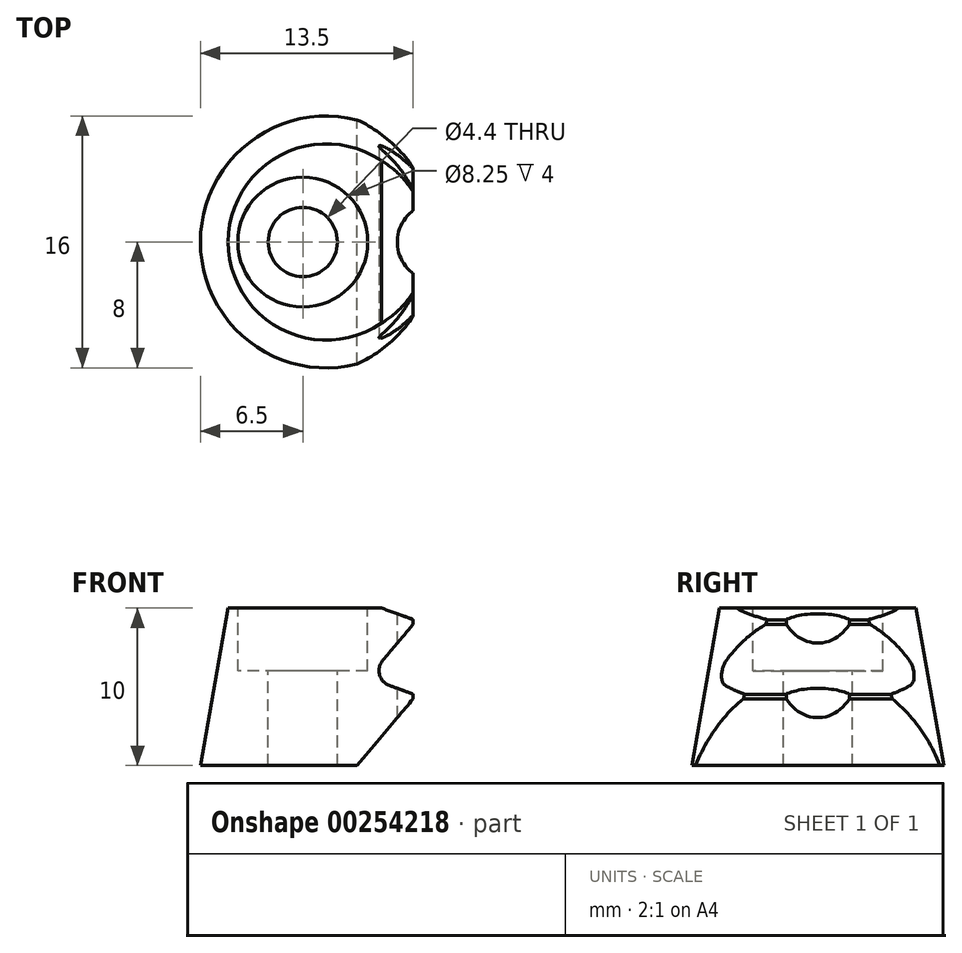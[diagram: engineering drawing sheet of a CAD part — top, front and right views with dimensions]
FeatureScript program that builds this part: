
annotation { "Feature Type Name" : "Feature", "Feature Type Description" : "" }
export const myFeature = defineFeature(function(context is Context, id is Id, definition is map)
    precondition{}
    {
        {
            var Q0;
            Q0=qCreatedBy(makeId("Top.planeOp"),FACE);
            var sketch = newSketch(context, id + "F0", { "sketchPlane" : qUnion([Q0])});
            skCircle(sketch, "E0", {"center": v(0, 0) * mm, "radius": 8 * mm});
            skSolve(sketch);
        }
        {
            var Q0;
            Q0=makeQuery(id+"F0.imprint","IMPRINT",FACE,{"disambiguationData":[TD([[makeQuery(id+"F0.imprint","IMPRINT",EDGE,{"derivedFrom":sQuery(id+"F0.wireOp",EDGE,"E0")}),1.0]])]});
            extrude(context, id + "F1", {"entities" : qUnion([Q0]), "depth" : 10 * mm, "hasDraft" : true, "draftAngle" : 10 * degree, "draftPullDirection" : true});
        }
        {
            var Q0;
            Q0=makeQuery(id+"F1.opExtrude","CAP_FACE",FACE,{"disambiguationData":[OSD([sQuery(id+"F0.wireOp",EDGE,"E0")])],"isStart":true});
            var sketch = newSketch(context, id + "F2", { "sketchPlane" : qUnion([Q0])});
            skLineSegment(sketch, "E1.bottom", {"start": v(5.5, 15.05) * mm, "end": v(20.77, 15.05) * mm});
            skLineSegment(sketch, "E1.top", {"start": v(5.5, -16.77) * mm, "end": v(20.77, -16.77) * mm});
            skLineSegment(sketch, "E1.left", {"start": v(5.5, 15.05) * mm, "end": v(5.5, -16.77) * mm});
            skLineSegment(sketch, "E1.right", {"start": v(20.77, 15.05) * mm, "end": v(20.77, -16.77) * mm});
            skSolve(sketch);
        }
        {
            var Q0;
            {var subQ0=sQuery(id+"F2.wireOp",EDGE,"E1.left");var subQ1=makeQuery(id+"F1.opExtrude","CAP_EDGE",EDGE,{"disambiguationData":[OSD([sQuery(id+"F0.wireOp",EDGE,"E0")])],"isStart":true});var subQ2=makeQuery(id+"F2.imprint","INTERSECT",VERTEX,{"disambiguationData":[OD(0.0)],"derivedFrom":[subQ1,subQ0]});Q0=makeQuery(id+"F2.imprint","IMPRINT",FACE,{"disambiguationData":[TD([[makeQuery(id+"F2.imprint","IMPRINT",EDGE,{"disambiguationData":[TD([[subQ2,-1.0]])],"derivedFrom":subQ0}),1.0]])]});}
            extrude(context, id + "F3", {"entities" : qUnion([Q0]), "operationType" : NewBodyOperationType.REMOVE, "oppositeDirection" : true, "depth" : 25 * mm});
        }
        {
            var Q0;
            Q0=makeQuery(id+"F1.opExtrude","CAP_FACE",FACE,{"disambiguationData":[OSD([sQuery(id+"F0.wireOp",EDGE,"E0")])],"isStart":false});
            var sketch = newSketch(context, id + "F4", { "sketchPlane" : qUnion([Q0])});
            skPoint(sketch, "E2", {"position": v(-1.5, 0) * mm});
            skSolve(sketch);
        }
        {
            var Q0;
            Q0=sQuery(id+"F4.wireOp",VERTEX,"E2");
            var Q1;
            Q1=makeQuery(id+"F1.opExtrude","SWEPT_BODY",BODY,{"disambiguationData":[OSD([sQuery(id+"F0.wireOp",EDGE,"E0")])]});
            hole(context, id + "F5", {"style" : HoleStyle.C_BORE, "endStyle" : HoleEndStyle.THROUGH, "standardTappedOrClearance" : lookupTablePath({ "standard" : "ISO", "fit" : "Normal", "size" : "M4", "type" : "Clearance" }), "standardBlindInLast" : lookupTablePath({ "fit" : "Standard", "standard" : "ISO", "size" : "M4", "type" : "Clearance" }), "holeDiameter" : 4.4 * mm, "cBoreDiameter" : 8.25 * mm, "cBoreDepth" : 4 * mm, "tappedDepth" : 7.5 * mm, "tapClearance" : 3, "locations" : qUnion([Q0]), "scope" : qUnion([Q1])});
        }
        {
            var Q0;
            Q0=makeQuery(id+"F1.opExtrude","CAP_FACE",FACE,{"disambiguationData":[OSD([sQuery(id+"F0.wireOp",EDGE,"E0")])],"isStart":false});
            var sketch = newSketch(context, id + "F6", { "sketchPlane" : qUnion([Q0])});
            skPoint(sketch, "E3", {"position": v(7, 0) * mm});
            skPoint(sketch, "E3.positionSnap0", {"position": v(5.5, 0) * mm});
            skSolve(sketch);
        }
        {
            var Q0;
            Q0=sQuery(id+"F6.wireOp",VERTEX,"E3");
            var Q1;
            Q1=makeQuery(id+"F1.opExtrude","SWEPT_BODY",BODY,{"disambiguationData":[OSD([sQuery(id+"F0.wireOp",EDGE,"E0")])]});
            hole(context, id + "F7", {"style" : HoleStyle.SIMPLE, "endStyle" : HoleEndStyle.THROUGH, "holeDiameter" : 5 * mm, "tappedDepth" : 7.5 * mm, "tapClearance" : 3, "locations" : qUnion([Q0]), "scope" : qUnion([Q1])});
        }
        {
            var Q0;
            Q0=qCreatedBy(makeId("Front.planeOp"),FACE);
            var sketch = newSketch(context, id + "F8", { "sketchPlane" : qUnion([Q0])});
            skLineSegment(sketch, "E4", {"start": v(3.5, 10) * mm, "end": v(5.43, 9.3) * mm});
            skLineSegment(sketch, "E5", {"start": v(5.52, 8.98) * mm, "end": v(2.66, 5.57) * mm});
            skLineSegment(sketch, "E6", {"start": v(2.66, 5.57) * mm, "end": v(5.43, 4.56) * mm});
            skLineSegment(sketch, "E7", {"start": v(5.52, 4.24) * mm, "end": v(0.78, -1.4) * mm});
            skLineSegment(sketch, "E8", {"start": v(0.78, -1.4) * mm, "end": v(10.43, -1.4) * mm});
            skLineSegment(sketch, "E9", {"start": v(10.43, -1.4) * mm, "end": v(10.43, 10) * mm});
            skLineSegment(sketch, "E10", {"start": v(10.43, 10) * mm, "end": v(3.5, 10) * mm});
            skPoint(sketch, "E11.visualSharp", {"position": v(5.7, 9.2) * mm});
            skArc(sketch, "E11.filletArc", {"start": v(5.52, 8.98) * mm, "mid": v(5.56, 9.16) * mm, "end": v(5.43, 9.3) * mm});
            skPoint(sketch, "E12.visualSharp", {"position": v(5.7, 4.46) * mm});
            skArc(sketch, "E12.filletArc", {"start": v(5.52, 4.24) * mm, "mid": v(5.56, 4.42) * mm, "end": v(5.43, 4.56) * mm});
            skSolve(sketch);
        }
        {
            var Q0;
            Q0=makeQuery(id+"F8.imprint","IMPRINT",FACE,{"disambiguationData":[TD([[makeQuery(id+"F8.imprint","IMPRINT",EDGE,{"derivedFrom":sQuery(id+"F8.wireOp",EDGE,"E4")}),1.0]])]});
            extrude(context, id + "F9", {"entities" : qUnion([Q0]), "operationType" : NewBodyOperationType.REMOVE, "endBound" : BoundingType.SYMMETRIC, "depth" : 25 * mm});
        }
        {
            var Q0;
            Q0=makeQuery(id+"F9.boolean.opBoolean","COPY",EDGE,{"derivedFrom":makeQuery(id+"F9.opExtrude","SWEPT_EDGE",EDGE,{"disambiguationData":[OSD([sQuery(id+"F8.wireOp",EDGE,"E5"),sQuery(id+"F8.wireOp",EDGE,"E6")])]})});
            fillet(context, id + "F10", {"entities" : qUnion([Q0]), "radius" : 1 * mm, "tangentPropagation" : true, "allowEdgeOverflow" : false});
        }
    });
